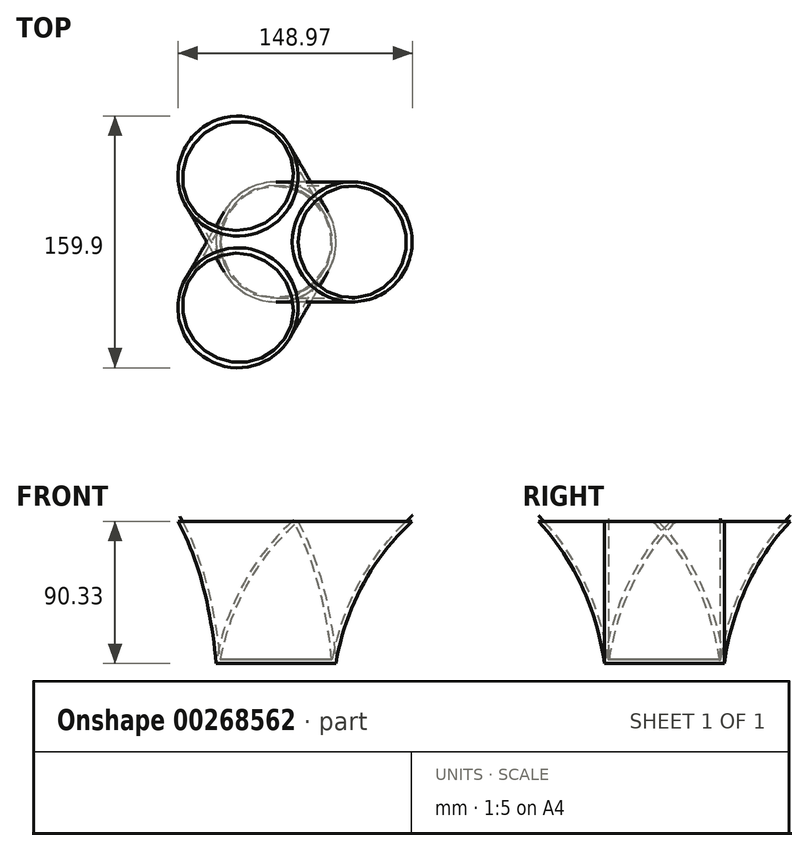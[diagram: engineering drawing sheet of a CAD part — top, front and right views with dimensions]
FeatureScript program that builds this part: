
annotation { "Feature Type Name" : "Feature", "Feature Type Description" : "" }
export const myFeature = defineFeature(function(context is Context, id is Id, definition is map)
    precondition{}
    {
        {
            var Q0;
            Q0=qCreatedBy(makeId("Top.planeOp"),FACE);
            var sketch = newSketch(context, id + "F0", { "sketchPlane" : qUnion([Q0])});
            skCircle(sketch, "E0", {"center": v(0, 0) * mm, "radius": 38.1 * mm});
            skSolve(sketch);
        }
        {
            var Q0;
            Q0=qCreatedBy(makeId("Front.planeOp"),FACE);
            var sketch = newSketch(context, id + "F1", { "sketchPlane" : qUnion([Q0])});
            skArc(sketch, "E1", {"start": v(48.32, 90.33) * mm, "mid": v(16.6, 49.21) * mm, "end": v(0, 0) * mm});
            skSolve(sketch);
        }
        {
            var Q0;
            Q0=makeQuery(id+"F0.imprint","IMPRINT",FACE,{"disambiguationData":[TD([[makeQuery(id+"F0.imprint","IMPRINT",EDGE,{"derivedFrom":sQuery(id+"F0.wireOp",EDGE,"E0")}),1.0]])]});
            var Q1;
            Q1=sQuery(id+"F1.wireOp",EDGE,"E1");
            sweep(context, id + "F2", {"profiles" : qUnion([Q0]), "path" : qUnion([Q1]), "keepProfileOrientation" : true});
        }
        {
            var Q0;
            Q0=makeQuery(id+"F2.opSweep","SWEPT_BODY",BODY,{"disambiguationData":[OSD([sQuery(id+"F0.wireOp",EDGE,"E0"),sQuery(id+"F1.wireOp",EDGE,"E1")])]});
            var Q1;
            Q1=makeQuery(id+"F2.opSweep","CAP_EDGE",EDGE,{"disambiguationData":[OSD([sQuery(id+"F0.wireOp",EDGE,"E0"),sQuery(id+"F1.wireOp",VERTEX,"E1.end")])],"isStart":true});
            circularPattern(context, id + "F3", {"entities" : qUnion([Q0]), "axis" : qUnion([Q1]), "angle" : 360 * degree, "instanceCount" : 3, "equalSpace" : true});
        }
        {
            var Q0;
            Q0=makeQuery(id+"F3.opPattern","COPY",FACE,{"derivedFrom":makeQuery(id+"F2.opSweep","CAP_FACE",FACE,{"disambiguationData":[OSD([sQuery(id+"F0.wireOp",EDGE,"E0"),sQuery(id+"F1.wireOp",VERTEX,"E1.start")])],"isStart":false}),"instanceName":"1"});
            var Q1;
            Q1=makeQuery(id+"F2.opSweep","CAP_FACE",FACE,{"disambiguationData":[OSD([sQuery(id+"F0.wireOp",EDGE,"E0"),sQuery(id+"F1.wireOp",VERTEX,"E1.start")])],"isStart":false});
            var Q2;
            Q2=makeQuery(id+"F3.opPattern","COPY",FACE,{"derivedFrom":makeQuery(id+"F2.opSweep","CAP_FACE",FACE,{"disambiguationData":[OSD([sQuery(id+"F0.wireOp",EDGE,"E0"),sQuery(id+"F1.wireOp",VERTEX,"E1.start")])],"isStart":false}),"instanceName":"2"});
            shell(context, id + "F4", {"entities" : qUnion([Q0, Q1, Q2]), "thickness" : 2.54 * mm});
        }
    });
